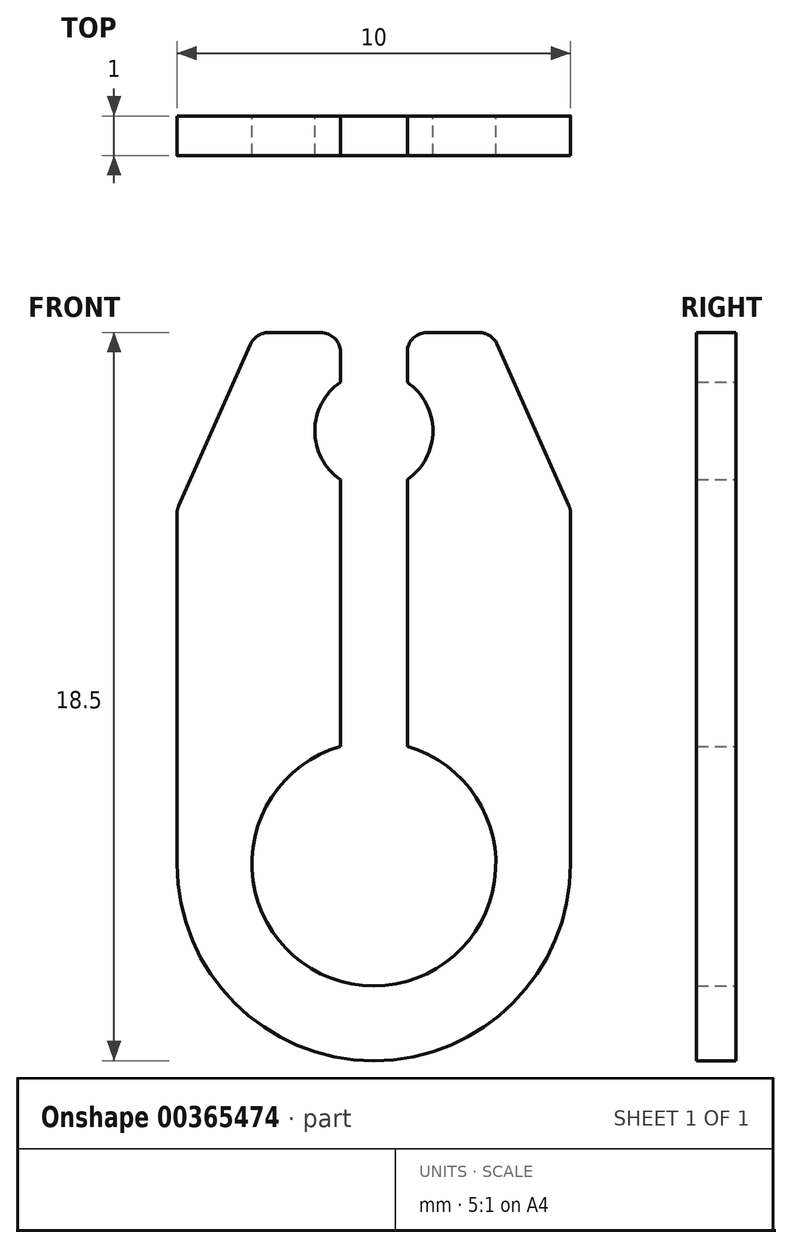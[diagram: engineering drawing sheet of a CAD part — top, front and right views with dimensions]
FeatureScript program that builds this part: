
annotation { "Feature Type Name" : "Feature", "Feature Type Description" : "" }
export const myFeature = defineFeature(function(context is Context, id is Id, definition is map)
    precondition{}
    {
        {
            var Q0;
            Q0=qCreatedBy(makeId("Front.planeOp"),FACE);
            var sketch = newSketch(context, id + "F0", { "sketchPlane" : qUnion([Q0])});
            skArc(sketch, "E0", {"start": v(-0.85, 2.98) * mm, "mid": v(0, -3.1) * mm, "end": v(0.85, 2.98) * mm});
            skArc(sketch, "E1", {"start": v(-0.85, 12.24) * mm, "mid": v(-1.5, 11) * mm, "end": v(-0.85, 9.76) * mm});
            skLineSegment(sketch, "E2", {"start": v(0, 12.5) * mm, "end": v(0, 13.5) * mm});
            skLineSegment(sketch, "E3", {"start": v(-0.85, 13.5) * mm, "end": v(-3, 13.5) * mm});
            skLineSegment(sketch, "E4", {"start": v(-5, 0) * mm, "end": v(-5, 9) * mm});
            skLineSegment(sketch, "E5", {"start": v(-5, 9) * mm, "end": v(-3, 13.5) * mm});
            skLineSegment(sketch, "E6.MirrorCS", {"start": v(5, 0) * mm, "end": v(5, 9) * mm});
            skLineSegment(sketch, "E7.MirrorCS", {"start": v(5, 9) * mm, "end": v(3, 13.5) * mm});
            skLineSegment(sketch, "E8.MirrorCS", {"start": v(0.85, 13.5) * mm, "end": v(3, 13.5) * mm});
            skLineSegment(sketch, "E9", {"start": v(-0.85, 2.98) * mm, "end": v(-0.85, 9.76) * mm});
            skLineSegment(sketch, "E10", {"start": v(0.85, 13.5) * mm, "end": v(0.85, 12.24) * mm});
            skArc(sketch, "E11.trimOffspring", {"start": v(-5, 0) * mm, "mid": v(0, -5) * mm, "end": v(5, 0) * mm});
            skPoint(sketch, "E12.orphan", {"position": v(0, 13.5) * mm});
            skLineSegment(sketch, "E13.trimOffspring", {"start": v(-0.85, 12.24) * mm, "end": v(-0.85, 13.5) * mm});
            skLineSegment(sketch, "E14.trimOffspring", {"start": v(0.85, 9.76) * mm, "end": v(0.85, 2.98) * mm});
            skArc(sketch, "E15.trimOffspring", {"start": v(0.85, 9.76) * mm, "mid": v(1.5, 11) * mm, "end": v(0.85, 12.24) * mm});
            skSolve(sketch);
        }
        {
            var Q0;
            Q0=qSketchRegion(id+"F0",true);
            extrude(context, id + "F1", {"entities" : qUnion([Q0]), "depth" : 1 * mm});
        }
        {
            var Q0;
            Q0=makeQuery(id+"F1.opExtrude","SWEPT_EDGE",EDGE,{"disambiguationData":[OSD([sQuery(id+"F0.wireOp",EDGE,"E7.MirrorCS"),sQuery(id+"F0.wireOp",EDGE,"E8.MirrorCS")])]});
            var Q1;
            Q1=makeQuery(id+"F1.opExtrude","SWEPT_EDGE",EDGE,{"disambiguationData":[OSD([sQuery(id+"F0.wireOp",EDGE,"E8.MirrorCS"),sQuery(id+"F0.wireOp",EDGE,"E10")])]});
            var Q2;
            Q2=makeQuery(id+"F1.opExtrude","SWEPT_EDGE",EDGE,{"disambiguationData":[OSD([sQuery(id+"F0.wireOp",EDGE,"E3"),sQuery(id+"F0.wireOp",EDGE,"E13.trimOffspring")])]});
            var Q3;
            Q3=makeQuery(id+"F1.opExtrude","SWEPT_EDGE",EDGE,{"disambiguationData":[OSD([sQuery(id+"F0.wireOp",EDGE,"E3"),sQuery(id+"F0.wireOp",EDGE,"E5")])]});
            var Q4;
            Q4=makeQuery(id+"F1.opExtrude","SWEPT_EDGE",EDGE,{"disambiguationData":[OSD([sQuery(id+"F0.wireOp",EDGE,"E4"),sQuery(id+"F0.wireOp",EDGE,"E5")])]});
            var Q5;
            Q5=makeQuery(id+"F1.opExtrude","SWEPT_EDGE",EDGE,{"disambiguationData":[OSD([sQuery(id+"F0.wireOp",EDGE,"E6.MirrorCS"),sQuery(id+"F0.wireOp",EDGE,"E7.MirrorCS")])]});
            fillet(context, id + "F2", {"entities" : qUnion([Q0, Q1, Q2, Q3, Q4, Q5]), "radius" : 0.5 * mm, "tangentPropagation" : true, "allowEdgeOverflow" : false});
        }
    });
